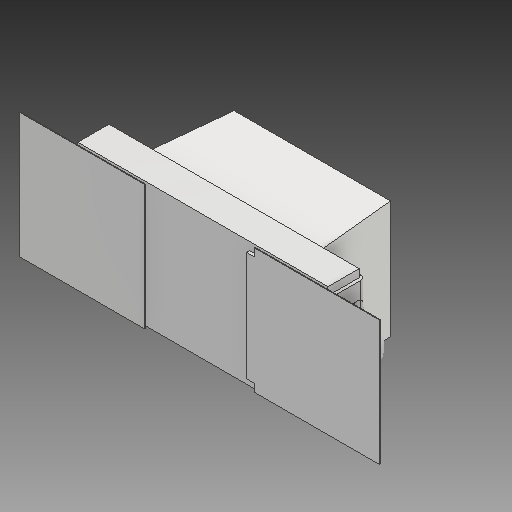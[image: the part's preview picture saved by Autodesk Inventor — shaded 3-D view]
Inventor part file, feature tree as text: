
AUTODESK INVENTOR PART (.ipt)
format: ipt  version: 2018 (Build 220112000, 112)  size: 244,224 bytes
history: native  units: mm
features: other x1, fillet x1
ambient origin geometry x8: Origin, YZ Plane, XZ Plane, XY Plane, X Axis, Y Axis, Z Axis, Center Point
bodies: Volumenkörper1 (feature_tree), Volumenkörper2 (feature_tree)
feature tree (2):
  other  "Boss-Extrude5"
  fillet  "Fillet3"  [1 undecoded]
note: 1 required parameter value undecoded (feature->parameter linkage not recoverable at this tier; creation-order binding heuristic only, values carry confidence <= 0.55)
